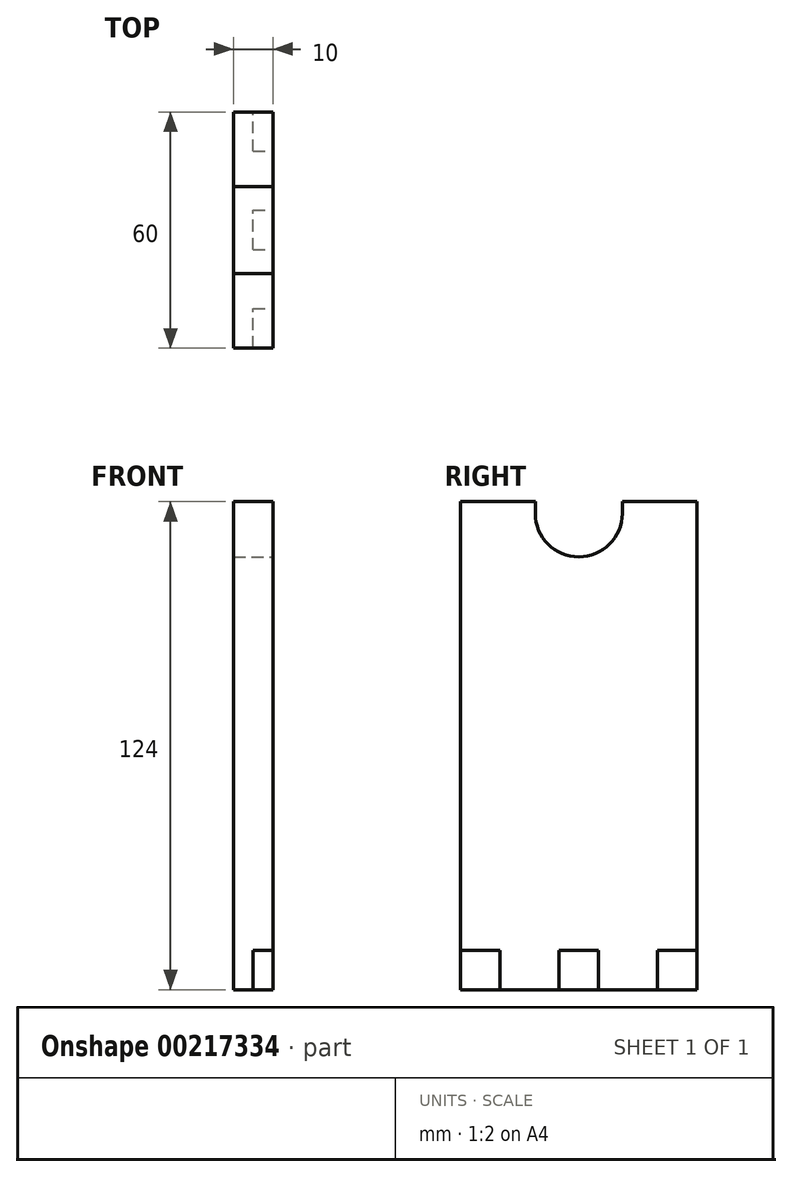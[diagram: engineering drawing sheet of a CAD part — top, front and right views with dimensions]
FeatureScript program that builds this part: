
annotation { "Feature Type Name" : "Feature", "Feature Type Description" : "" }
export const myFeature = defineFeature(function(context is Context, id is Id, definition is map)
    precondition{}
    {
        {
            var Q0;
            Q0=qCreatedBy(makeId("Front.planeOp"),FACE);
            var sketch = newSketch(context, id + "F0", { "sketchPlane" : qUnion([Q0])});
            skLineSegment(sketch, "E0.bottom", {"start": v(5, 62) * mm, "end": v(-5, 62) * mm});
            skLineSegment(sketch, "E0.top", {"start": v(5, -62) * mm, "end": v(-5, -62) * mm});
            skLineSegment(sketch, "E0.left", {"start": v(5, 62) * mm, "end": v(5, -62) * mm});
            skLineSegment(sketch, "E0.right", {"start": v(-5, 62) * mm, "end": v(-5, -62) * mm});
            skPoint(sketch, "E0.middle", {"position": v(0, 0) * mm});
            skSolve(sketch);
        }
        {
            var Q0;
            Q0=makeQuery(id+"F0.imprint","IMPRINT",FACE,{"disambiguationData":[TD([[makeQuery(id+"F0.imprint","IMPRINT",EDGE,{"derivedFrom":sQuery(id+"F0.wireOp",EDGE,"E0.bottom")}),1.0]])]});
            extrude(context, id + "F1", {"entities" : qUnion([Q0]), "endBound" : BoundingType.SYMMETRIC, "depth" : 60 * mm});
        }
        {
            var Q0;
            Q0=makeQuery(id+"F1.opExtrude","SWEPT_FACE",FACE,{"disambiguationData":[OSD([sQuery(id+"F0.wireOp",EDGE,"E0.left")])]});
            var sketch = newSketch(context, id + "F2", { "sketchPlane" : qUnion([Q0])});
            skArc(sketch, "E1", {"start": v(-11.05, 59) * mm, "mid": v(0, 47.95) * mm, "end": v(11.05, 59) * mm});
            skPoint(sketch, "E2", {"position": v(0, 62) * mm});
            skLineSegment(sketch, "E3", {"start": v(-11.05, 62) * mm, "end": v(-11.05, 59) * mm});
            skLineSegment(sketch, "E4", {"start": v(11.05, 62) * mm, "end": v(11.05, 59) * mm});
            skLineSegment(sketch, "E5", {"start": v(-11.05, 62) * mm, "end": v(11.05, 62) * mm});
            skSolve(sketch);
        }
        {
            var Q0;
            Q0=makeQuery(id+"F2.imprint","IMPRINT",FACE,{"disambiguationData":[TD([[makeQuery(id+"F2.imprint","IMPRINT",EDGE,{"derivedFrom":sQuery(id+"F2.wireOp",EDGE,"E1")}),1.0]])]});
            extrude(context, id + "F3", {"entities" : qUnion([Q0]), "operationType" : NewBodyOperationType.REMOVE, "oppositeDirection" : true, "depth" : 10 * mm});
        }
        {
            var Q0;
            Q0=makeQuery(id+"F1.opExtrude","SWEPT_FACE",FACE,{"disambiguationData":[OSD([sQuery(id+"F0.wireOp",EDGE,"E0.left")])]});
            var sketch = newSketch(context, id + "F4", { "sketchPlane" : qUnion([Q0])});
            skLineSegment(sketch, "E6.bottom", {"start": v(-30, -62) * mm, "end": v(-20, -62) * mm});
            skLineSegment(sketch, "E6.top", {"start": v(-30, -52) * mm, "end": v(-20, -52) * mm});
            skLineSegment(sketch, "E6.left", {"start": v(-30, -62) * mm, "end": v(-30, -52) * mm});
            skLineSegment(sketch, "E6.right", {"start": v(-20, -62) * mm, "end": v(-20, -52) * mm});
            skLineSegment(sketch, "E7.bottom", {"start": v(30, -62) * mm, "end": v(20, -62) * mm});
            skLineSegment(sketch, "E7.top", {"start": v(30, -52) * mm, "end": v(20, -52) * mm});
            skLineSegment(sketch, "E7.left", {"start": v(30, -62) * mm, "end": v(30, -52) * mm});
            skLineSegment(sketch, "E7.right", {"start": v(20, -62) * mm, "end": v(20, -52) * mm});
            skLineSegment(sketch, "E8.bottom", {"start": v(-5, -62) * mm, "end": v(5, -62) * mm});
            skLineSegment(sketch, "E8.top", {"start": v(-5, -52) * mm, "end": v(5, -52) * mm});
            skLineSegment(sketch, "E8.left", {"start": v(-5, -62) * mm, "end": v(-5, -52) * mm});
            skLineSegment(sketch, "E8.right", {"start": v(5, -62) * mm, "end": v(5, -52) * mm});
            skSolve(sketch);
        }
        {
            var Q0;
            Q0=makeQuery(id+"F4.imprint","IMPRINT",FACE,{"disambiguationData":[TD([[makeQuery(id+"F4.imprint","IMPRINT",EDGE,{"derivedFrom":sQuery(id+"F4.wireOp",EDGE,"E6.bottom")}),1.0]])]});
            var Q1;
            Q1=makeQuery(id+"F4.imprint","IMPRINT",FACE,{"disambiguationData":[TD([[makeQuery(id+"F4.imprint","IMPRINT",EDGE,{"derivedFrom":sQuery(id+"F4.wireOp",EDGE,"E7.bottom")}),1.0]])]});
            var Q2;
            Q2=makeQuery(id+"F4.imprint","IMPRINT",FACE,{"disambiguationData":[TD([[makeQuery(id+"F4.imprint","IMPRINT",EDGE,{"derivedFrom":sQuery(id+"F4.wireOp",EDGE,"E8.bottom")}),1.0]])]});
            extrude(context, id + "F5", {"entities" : qUnion([Q0, Q1, Q2]), "operationType" : NewBodyOperationType.REMOVE, "oppositeDirection" : true, "depth" : 5 * mm});
        }
    });
